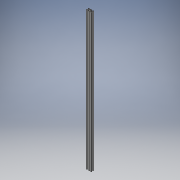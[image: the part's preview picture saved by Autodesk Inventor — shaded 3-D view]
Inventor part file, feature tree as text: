
AUTODESK INVENTOR PART (.ipt)
format: ipt  version: 2018 (Build 220112000, 112)  size: 203,776 bytes
history: native  units: mm
features: other x1, extrude x1, sketch x1
ambient origin geometry x8: Origin, YZ Plane, XZ Plane, XY Plane, X Axis, Y Axis, Z Axis, Center Point
bodies: Body1 (feature_tree)
feature tree (3):
  other  "Sólido1"
  extrude  "Extrusão1"  [1 undecoded]
  sketch  "Esboço1"  dims[d0=1054.0mm d1=0.0mm]
note: 1 required parameter value undecoded (feature->parameter linkage not recoverable at this tier; creation-order binding heuristic only, values carry confidence <= 0.55)
